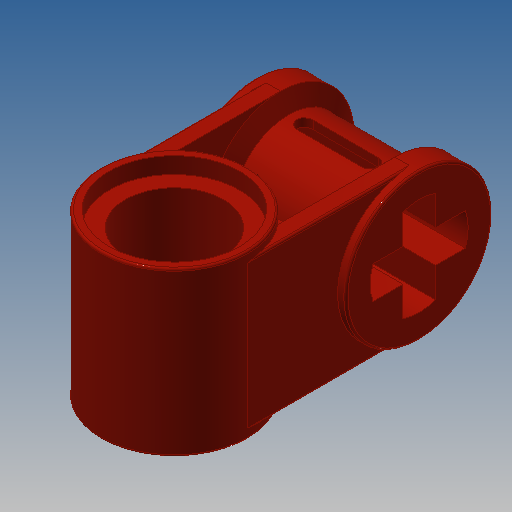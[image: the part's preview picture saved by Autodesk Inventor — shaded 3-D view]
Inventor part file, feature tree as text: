
AUTODESK INVENTOR PART (.ipt)
format: ipt  version: 2022.2 (Build 262287000, 287)  size: 271,360 bytes
history: native  units: in
note: dims shown in document units (in); Inventor stores cm internally (conversion verified against a paired STEP export)
features: extrude x6, sketch x4, mirror x1, plane x1, revolve x1, fillet x1
ambient origin geometry x8: Origin, YZ Plane, XZ Plane, XY Plane, X Axis, Y Axis, Z Axis, Center Point
bodies: Solid1 (feature_tree)
feature tree (14):
  sketch  "Sketch2"  dims[d0=0.2835in d1=0.189in]
  extrude  "Extrusion1"  Depth=0.189in
  extrude  "Extrusion3"  Depth=0.315in TaperAngle=0.0deg
  mirror  "Mirror1"
  plane  "Work Plane1"
  extrude  "Extrusion2"  Depth=0.2835in
  revolve  "Revolution1"  [1 undecoded]
  extrude  "Extrusion4"  Depth=0.0039in
  extrude  "Extrusion5"  Depth=0.0039in TaperAngle=0.0deg
  extrude  "Extrusion6"  Depth=0.0039in
  fillet  "Fillet1"  Radius=0.0472in
  sketch  "Sketch3"  dims[d2=0.315in d3=0.315in d4=0.0in]
  sketch  "Sketch4"  dims[d5=0.0in d6=0.2835in]
  sketch  "Sketch5"  dims[d7=0.0315in d8=0.315in d9=0.0in d10=0.252in d11=0.0315in d12=0.0in d13=0.2835in d14=0.0472in d15=0.315in d16=0.2205in d17=0.063in d18=0.0315in d19=0.1575in d20=90.0deg d21=0.063in d22=0.0in d23=0.063in d24=0.0in d25=0.189in d26=0.063in d27=0.063in d28=0.0in d29=0.0039in]
note: 1 required parameter value undecoded (feature->parameter linkage not recoverable at this tier; creation-order binding heuristic only, values carry confidence <= 0.55)
